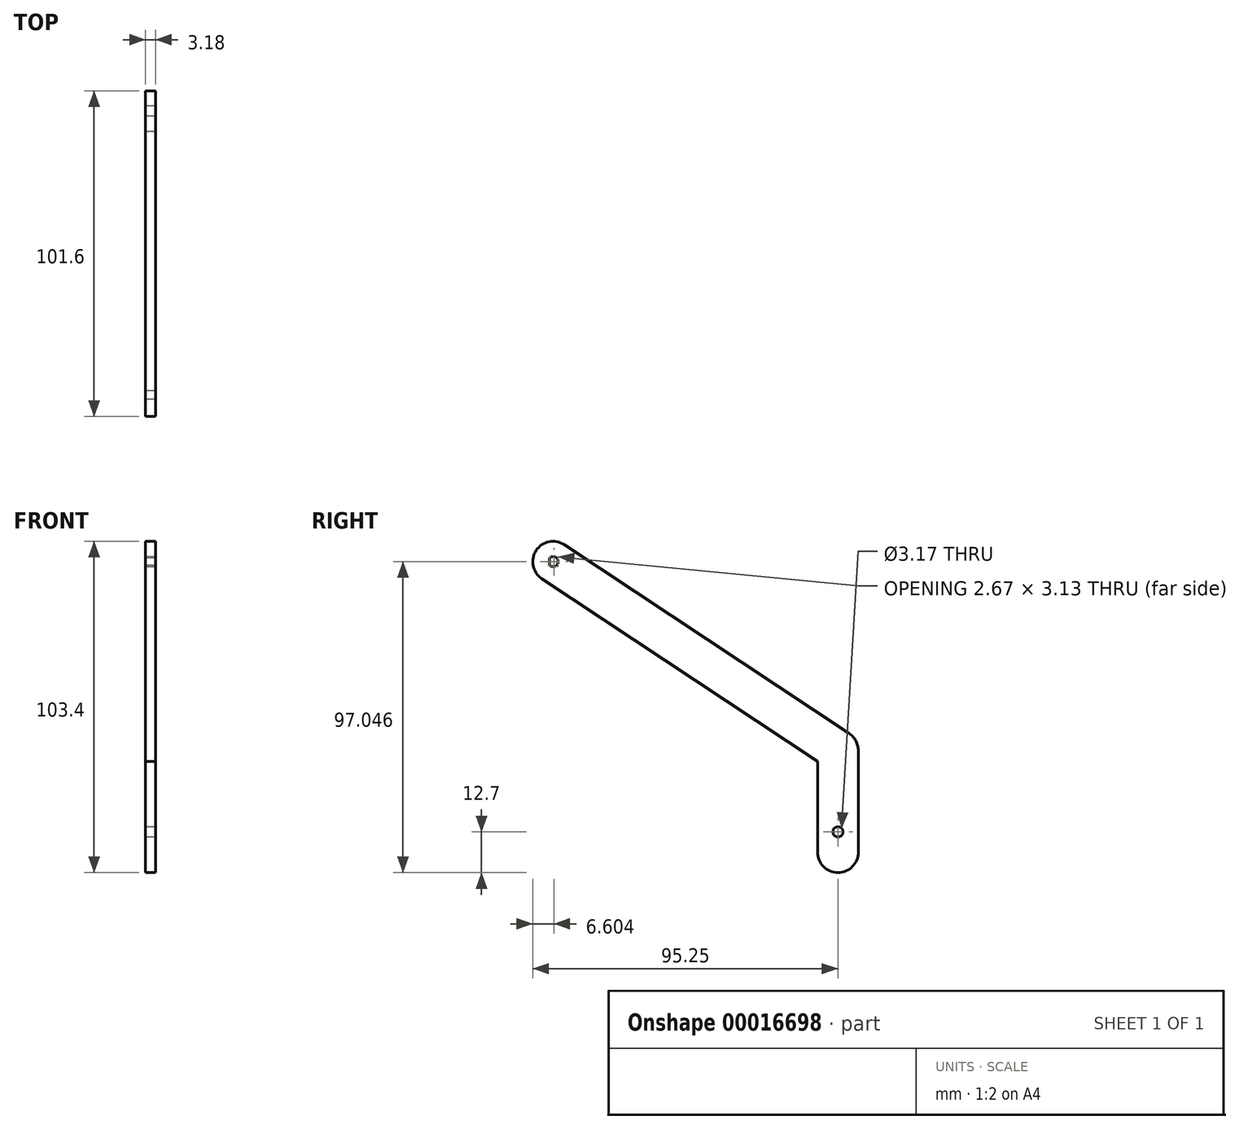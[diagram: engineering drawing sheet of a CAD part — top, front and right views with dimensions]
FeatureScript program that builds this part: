
annotation { "Feature Type Name" : "Feature", "Feature Type Description" : "" }
export const myFeature = defineFeature(function(context is Context, id is Id, definition is map)
    precondition{}
    {
        {
            var Q0;
            Q0=qCreatedBy(makeId("Right.planeOp"),FACE);
            var sketch = newSketch(context, id + "F0", { "sketchPlane" : qUnion([Q0])});
            skLineSegment(sketch, "E0", {"start": v(0, 0) * mm, "end": v(-88.9, 90.7) * mm, "construction": true});
            skLineSegment(sketch, "E1", {"start": v(-88.9, 90.7) * mm, "end": v(-88.9, 0) * mm, "construction": true});
            skLineSegment(sketch, "E2", {"start": v(-135.33, 14.5) * mm, "end": v(-48.02, 14.5) * mm, "construction": true});
            skArc(sketch, "E3", {"start": v(-84.37, 95.14) * mm, "mid": v(-93.35, 95.23) * mm, "end": v(-93.43, 86.25) * mm});
            skArc(sketch, "E4", {"start": v(-4.53, -4.45) * mm, "mid": v(4.45, -4.53) * mm, "end": v(4.53, 4.44) * mm});
            skLineSegment(sketch, "E5", {"start": v(-84.37, 95.14) * mm, "end": v(4.53, 4.44) * mm});
            skLineSegment(sketch, "E6", {"start": v(-4.53, -4.45) * mm, "end": v(-93.43, 86.25) * mm});
            skLineSegment(sketch, "E7", {"start": v(-84.37, 95.14) * mm, "end": v(-93.43, 86.25) * mm, "construction": true});
            skSolve(sketch);
        }
        {
            var Q0;
            Q0=qCreatedBy(makeId("Right.planeOp"),FACE);
            var sketch = newSketch(context, id + "F1", { "sketchPlane" : qUnion([Q0])});
            skArc(sketch, "E8", {"start": v(-6.35, 0) * mm, "mid": v(0, -6.35) * mm, "end": v(6.35, 0) * mm});
            skCircle(sketch, "E9", {"center": v(0, 6.35) * mm, "radius": 1.59 * mm});
            skLineSegment(sketch, "E10.left", {"start": v(6.35, 0) * mm, "end": v(6.35, 31.75) * mm});
            skLineSegment(sketch, "E10.right", {"start": v(-6.35, 0) * mm, "end": v(-6.35, 31.75) * mm});
            skLineSegment(sketch, "E11", {"start": v(0, 31.75) * mm, "end": v(-88.9, 90.7) * mm, "construction": true});
            skArc(sketch, "E12", {"start": v(-85.4, 95.99) * mm, "mid": v(-94.2, 94.2) * mm, "end": v(-92.4, 85.4) * mm});
            skLineSegment(sketch, "E13", {"start": v(-92.4, 85.4) * mm, "end": v(-3.5, 26.46) * mm});
            skLineSegment(sketch, "E14", {"start": v(-85.4, 95.99) * mm, "end": v(3.5, 37.04) * mm});
            skArc(sketch, "E15", {"start": v(-6.35, 31.75) * mm, "mid": v(3, 26.16) * mm, "end": v(3.5, 37.04) * mm});
            skArc(sketch, "E16", {"start": v(-3.5, 26.46) * mm, "mid": v(5.6, 34.75) * mm, "end": v(-6.35, 31.75) * mm});
            skArc(sketch, "E17", {"start": v(-89.98, 89.53) * mm, "mid": v(-87.31, 90.7) * mm, "end": v(-89.98, 91.86) * mm});
            skLineSegment(sketch, "E18", {"start": v(-89.98, 91.86) * mm, "end": v(-89.98, 89.53) * mm});
            skLineSegment(sketch, "E19.0", {"start": v(0, 0) * mm, "end": v(-88.9, 90.7) * mm, "construction": true});
            skSolve(sketch);
        }
        {
            var Q0;
            {var subQ6=sQuery(id+"F1.wireOp",EDGE,"E12");Q0=makeQuery(id+"F1.imprint","IMPRINT",FACE,{"disambiguationData":[TD([[makeQuery(id+"F1.imprint","IMPRINT",EDGE,{"derivedFrom":subQ6}),1.0]])]});}
            var Q1;
            {var subQ6=sQuery(id+"F1.wireOp",EDGE,"E8");Q1=makeQuery(id+"F1.imprint","IMPRINT",FACE,{"disambiguationData":[TD([[makeQuery(id+"F1.imprint","IMPRINT",EDGE,{"derivedFrom":subQ6}),1.0]])]});}
            var Q2;
            {var subQ2=sQuery(id+"F1.wireOp",EDGE,"E15");Q2=makeQuery(id+"F1.imprint","IMPRINT",FACE,{"disambiguationData":[TD([[makeQuery(id+"F1.imprint","IMPRINT",EDGE,{"derivedFrom":subQ2}),1.0]])]});}
            var Q3;
            {var subQ0=sQuery(id+"F1.wireOp",EDGE,"E15");Q3=makeQuery(id+"F1.imprint","IMPRINT",FACE,{"disambiguationData":[TD([[makeQuery(id+"F1.imprint","IMPRINT",EDGE,{"derivedFrom":subQ0}),-1.0]])]});}
            extrude(context, id + "F2", {"entities" : qUnion([Q0, Q1, Q2, Q3]), "depth" : 3.17 * mm});
        }
    });
